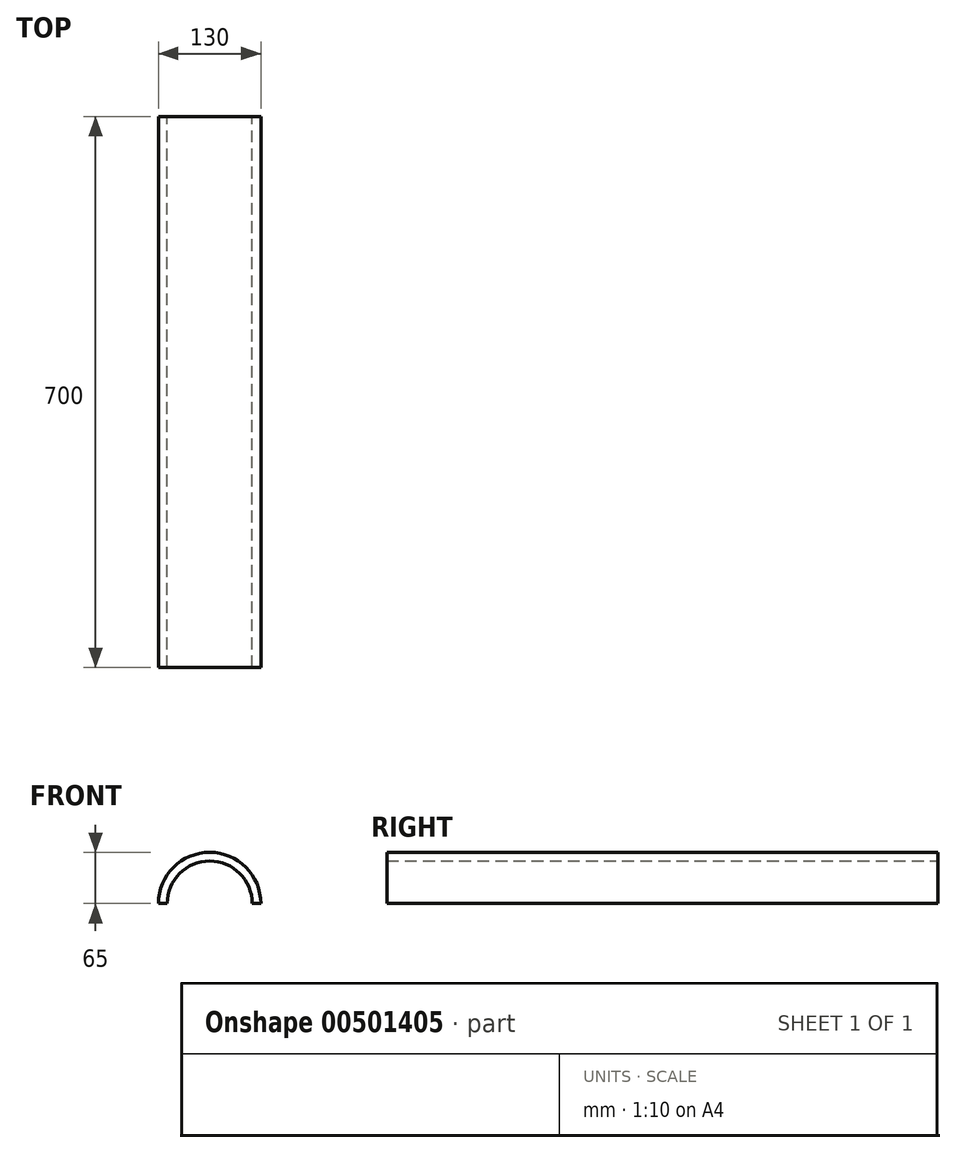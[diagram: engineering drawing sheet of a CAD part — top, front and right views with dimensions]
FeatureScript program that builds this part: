
annotation { "Feature Type Name" : "Feature", "Feature Type Description" : "" }
export const myFeature = defineFeature(function(context is Context, id is Id, definition is map)
    precondition{}
    {
        {
            var Q0;
            Q0=qCreatedBy(makeId("Front.planeOp"),FACE);
            var sketch = newSketch(context, id + "F0", { "sketchPlane" : qUnion([Q0])});
            skArc(sketch, "E0", {"start": v(54, 0) * mm, "mid": v(0, 54) * mm, "end": v(-54, 0) * mm});
            skArc(sketch, "E1", {"start": v(65, 0) * mm, "mid": v(0, 65) * mm, "end": v(-65, 0) * mm});
            skLineSegment(sketch, "E2", {"start": v(-65, 0) * mm, "end": v(-54, 0) * mm});
            skLineSegment(sketch, "E3", {"start": v(54, 0) * mm, "end": v(65, 0) * mm});
            skSolve(sketch);
        }
        {
            var Q0;
            Q0 = qSketchRegion(id + "F0", true);
            extrude(context, id + "F1", {"entities" : qUnion([Q0]), "depth" : 700 * mm});
        }
    });
